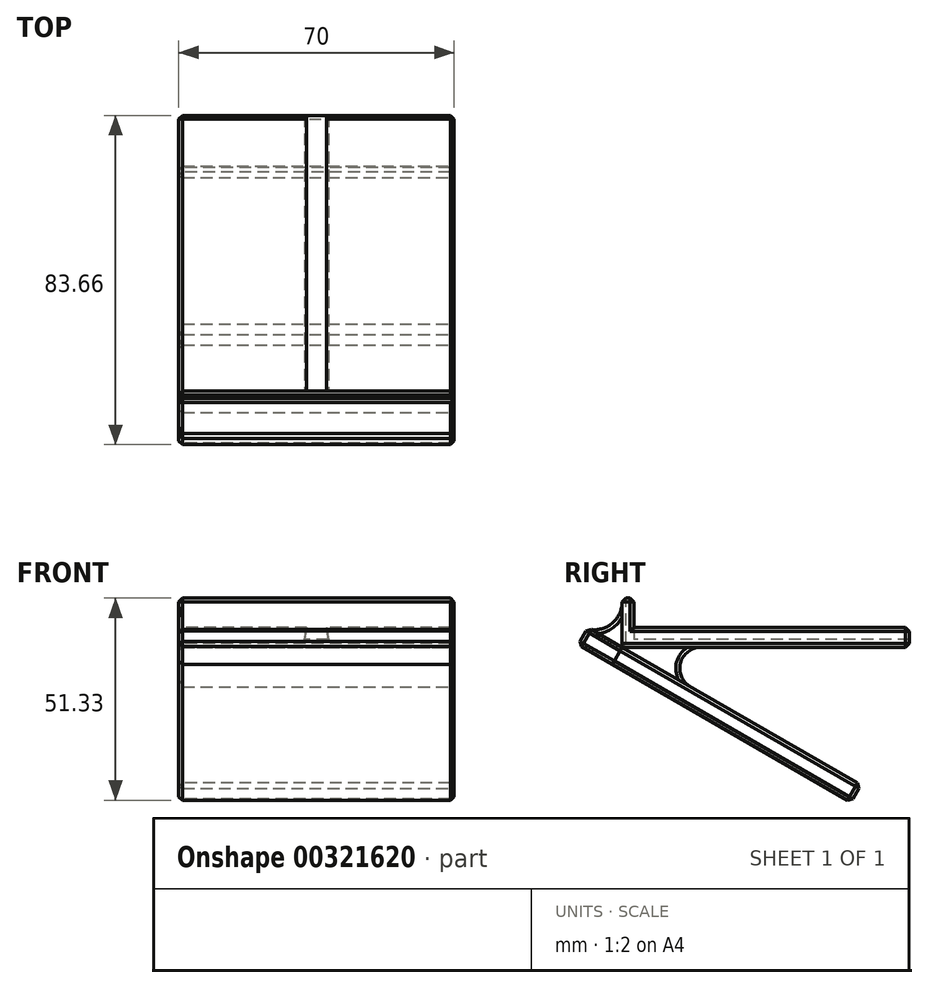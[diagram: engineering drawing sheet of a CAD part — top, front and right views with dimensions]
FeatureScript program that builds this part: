
annotation { "Feature Type Name" : "Feature", "Feature Type Description" : "" }
export const myFeature = defineFeature(function(context is Context, id is Id, definition is map)
    precondition{}
    {
        {
            var Q0;
            Q0=qCreatedBy(makeId("Top.planeOp"),FACE);
            var sketch = newSketch(context, id + "F0", { "sketchPlane" : qUnion([Q0])});
            skLineSegment(sketch, "E0.bottom", {"start": v(35, 35) * mm, "end": v(-35, 35) * mm});
            skLineSegment(sketch, "E0.top", {"start": v(35, -35) * mm, "end": v(-35, -35) * mm});
            skLineSegment(sketch, "E0.left", {"start": v(35, 35) * mm, "end": v(35, -35) * mm});
            skLineSegment(sketch, "E0.right", {"start": v(-35, 35) * mm, "end": v(-35, -35) * mm});
            skPoint(sketch, "E0.middle", {"position": v(0, 0) * mm});
            skSolve(sketch);
        }
        {
            var Q0;
            Q0=makeQuery(id+"F0.imprint","IMPRINT",FACE,{"disambiguationData":[TD([[makeQuery(id+"F0.imprint","IMPRINT",EDGE,{"derivedFrom":sQuery(id+"F0.wireOp",EDGE,"E0.bottom")}),1.0]])]});
            extrude(context, id + "F1", {"entities" : qUnion([Q0]), "depth" : 5 * mm});
        }
        {
            var Q0;
            Q0=makeQuery(id+"F1.opExtrude","SWEPT_FACE",FACE,{"disambiguationData":[OSD([sQuery(id+"F0.wireOp",EDGE,"E0.top")])]});
            var sketch = newSketch(context, id + "F2", { "sketchPlane" : qUnion([Q0])});
            skLineSegment(sketch, "E1", {"start": v(0, 5) * mm, "end": v(2.5, 5) * mm});
            skLineSegment(sketch, "E2", {"start": v(0, 2) * mm, "end": v(3, 2) * mm});
            skLineSegment(sketch, "E3", {"start": v(3, 2) * mm, "end": v(2.5, 5) * mm});
            skLineSegment(sketch, "E4", {"start": v(0, 2) * mm, "end": v(-3, 2) * mm});
            skLineSegment(sketch, "E5", {"start": v(0, 5) * mm, "end": v(-2.5, 5) * mm});
            skLineSegment(sketch, "E6", {"start": v(-2.5, 5) * mm, "end": v(-3, 2) * mm});
            skSolve(sketch);
        }
        {
            var Q0;
            Q0=makeQuery(id+"F2.imprint","IMPRINT",FACE,{"disambiguationData":[TD([[makeQuery(id+"F2.imprint","IMPRINT",EDGE,{"derivedFrom":sQuery(id+"F2.wireOp",EDGE,"E1")}),1.0]])]});
            var Q1;
            Q1=makeQuery(id+"F1.opExtrude","SWEPT_FACE",FACE,{"disambiguationData":[OSD([sQuery(id+"F0.wireOp",EDGE,"E0.bottom")])]});
            extrude(context, id + "F3", {"entities" : qUnion([Q0]), "operationType" : NewBodyOperationType.REMOVE, "endBound" : BoundingType.UP_TO_SURFACE, "oppositeDirection" : true, "endBoundEntityFace" : qUnion([Q1]), "depth" : 25 * mm});
        }
        {
            var Q0;
            Q0=makeQuery(id+"F1.opExtrude","SWEPT_FACE",FACE,{"disambiguationData":[OSD([sQuery(id+"F0.wireOp",EDGE,"E0.top")])]});
            var sketch = newSketch(context, id + "F4", { "sketchPlane" : qUnion([Q0])});
            skLineSegment(sketch, "E7.bottom", {"start": v(-35, 0) * mm, "end": v(35, 0) * mm});
            skLineSegment(sketch, "E7.top", {"start": v(-35, 12.5) * mm, "end": v(35, 12.5) * mm});
            skLineSegment(sketch, "E7.left", {"start": v(-35, 0) * mm, "end": v(-35, 12.5) * mm});
            skLineSegment(sketch, "E7.right", {"start": v(35, 0) * mm, "end": v(35, 12.5) * mm});
            skSolve(sketch);
        }
        {
            var Q0;
            Q0 = qSketchRegion(id + "F4", true);
            extrude(context, id + "F5", {"entities" : qUnion([Q0]), "operationType" : NewBodyOperationType.ADD, "depth" : 3 * mm});
        }
        {
            var Q0;
            Q0=makeQuery(id+"F5.opExtrude","CAP_EDGE",EDGE,{"disambiguationData":[OSD([sQuery(id+"F4.wireOp",EDGE,"E7.bottom")])],"isStart":false});
            var Q1;
            Q1=makeQuery(id+"F5.boolean.opBoolean","MERGE",EDGE,{"derivedFrom":[makeQuery(id+"F1.opExtrude","CAP_EDGE",EDGE,{"disambiguationData":[OSD([sQuery(id+"F0.wireOp",EDGE,"E0.left")])],"isStart":true}),makeQuery(id+"F5.opExtrude","SWEPT_EDGE",EDGE,{"disambiguationData":[OSD([sQuery(id+"F4.wireOp",EDGE,"E7.bottom"),sQuery(id+"F4.wireOp",EDGE,"E7.right")])]})]});
            cPlane(context, id + "F6", {"entities" : qUnion([Q0, Q1]), "cplaneType" : CPlaneType.LINE_ANGLE, "offset" : 25 * mm, "angle" : 30 * degree, "width" : 150 * mm, "height" : 150 * mm});
        }
        {
            var Q0;
            Q0=qCreatedBy(id+"F6.planeOp",FACE);
            var sketch = newSketch(context, id + "F7", { "sketchPlane" : qUnion([Q0])});
            skLineSegment(sketch, "E8.bottom", {"start": v(-35, -32.9) * mm, "end": v(35, -32.9) * mm});
            skLineSegment(sketch, "E8.top", {"start": v(-35, 37.1) * mm, "end": v(35, 37.1) * mm});
            skLineSegment(sketch, "E8.left", {"start": v(-35, -32.9) * mm, "end": v(-35, 37.1) * mm});
            skLineSegment(sketch, "E8.right", {"start": v(35, -32.9) * mm, "end": v(35, 37.1) * mm});
            skSolve(sketch);
        }
        {
            var Q0;
            Q0 = qSketchRegion(id + "F7", true);
            extrude(context, id + "F8", {"entities" : qUnion([Q0]), "operationType" : NewBodyOperationType.ADD, "oppositeDirection" : true, "depth" : 5 * mm});
        }
        {
            var Q0;
            Q0=makeQuery(id+"F8.opExtrude","SWEPT_FACE",FACE,{"disambiguationData":[OSD([sQuery(id+"F7.wireOp",EDGE,"E8.bottom")])]});
            extrude(context, id + "F9", {"entities" : qUnion([Q0]), "depth" : 10 * mm});
        }
        {
            var Q0;
            Q0=makeQuery(id+"F8.opExtrude","SWEPT_FACE",FACE,{"disambiguationData":[OSD([sQuery(id+"F7.wireOp",EDGE,"E8.right")])]});
            var sketch = newSketch(context, id + "F10", { "sketchPlane" : qUnion([Q0])});
            skLineSegment(sketch, "E9", {"start": v(-38, 0) * mm, "end": v(-20.68, -10) * mm});
            skLineSegment(sketch, "E10", {"start": v(-18, 0) * mm, "end": v(-38, 0) * mm});
            skLineSegment(sketch, "E11", {"start": v(-38, 0) * mm, "end": v(-45.8, 4.5) * mm});
            skLineSegment(sketch, "E12", {"start": v(-38, 0) * mm, "end": v(-38, 11.5) * mm});
            skArc(sketch, "E13", {"start": v(-45.8, 4.5) * mm, "mid": v(-40.34, 6.26) * mm, "end": v(-38, 11.5) * mm});
            skArc(sketch, "E14", {"start": v(-18, 0) * mm, "mid": v(-23.18, -3.97) * mm, "end": v(-20.68, -10) * mm});
            skSolve(sketch);
        }
        {
            var Q0;
            Q0 = qSketchRegion(id + "F10", true);
            var Q1;
            Q1=makeQuery(id+"F8.opExtrude","SWEPT_FACE",FACE,{"disambiguationData":[OSD([sQuery(id+"F7.wireOp",EDGE,"E8.left")])]});
            extrude(context, id + "F11", {"entities" : qUnion([Q0]), "endBound" : BoundingType.UP_TO_SURFACE, "oppositeDirection" : true, "endBoundEntityFace" : qUnion([Q1]), "depth" : 25 * mm});
        }
        {
            var Q0;
            Q0=makeQuery(id+"F9.opExtrude","CAP_EDGE",EDGE,{"disambiguationData":[OSD([sQuery(id+"F7.wireOp",EDGE,"E8.bottom"),sQuery(id+"F7.wireOp",EDGE,"E8.right")])],"isStart":false});
            var Q1;
            {var subQ0=sQuery(id+"F7.wireOp",EDGE,"E8.right");var subQ1=sQuery(id+"F7.wireOp",EDGE,"E8.bottom");Q1=makeQuery(id+"F9.opExtrude","SWEPT_EDGE",EDGE,{"disambiguationData":[OSD([subQ1,subQ0]),TDD([makeQuery(id+"F8.opExtrude","CAP_VERTEX",VERTEX,{"disambiguationData":[OSD([subQ1,subQ0])],"isStart":false})])]});}
            var Q2;
            Q2=makeQuery(id+"F8.opExtrude","CAP_EDGE",EDGE,{"disambiguationData":[OSD([sQuery(id+"F7.wireOp",EDGE,"E8.right")])],"isStart":false});
            var Q3;
            Q3=makeQuery(id+"F5.opExtrude","SWEPT_EDGE",EDGE,{"disambiguationData":[OSD([sQuery(id+"F4.wireOp",EDGE,"E7.top"),sQuery(id+"F4.wireOp",EDGE,"E7.right")])]});
            var Q4;
            Q4=makeQuery(id+"F5.opExtrude","CAP_EDGE",EDGE,{"disambiguationData":[OSD([sQuery(id+"F4.wireOp",EDGE,"E7.right")])],"isStart":true});
            var Q5;
            Q5=makeQuery(id+"F1.opExtrude","CAP_EDGE",EDGE,{"disambiguationData":[OSD([sQuery(id+"F0.wireOp",EDGE,"E0.left")])],"isStart":false});
            var Q6;
            Q6=makeQuery(id+"F1.opExtrude","SWEPT_EDGE",EDGE,{"disambiguationData":[OSD([sQuery(id+"F0.wireOp",EDGE,"E0.bottom"),sQuery(id+"F0.wireOp",EDGE,"E0.left")])]});
            var Q7;
            Q7=makeQuery(id+"F8.opExtrude","SWEPT_EDGE",EDGE,{"disambiguationData":[OSD([sQuery(id+"F7.wireOp",EDGE,"E8.top"),sQuery(id+"F7.wireOp",EDGE,"E8.right")])]});
            var Q8;
            Q8=makeQuery(id+"F5.opExtrude","CAP_EDGE",EDGE,{"disambiguationData":[OSD([sQuery(id+"F4.wireOp",EDGE,"E7.top")])],"isStart":false});
            var Q9;
            Q9=makeQuery(id+"F5.opExtrude","SWEPT_FACE",FACE,{"disambiguationData":[OSD([sQuery(id+"F4.wireOp",EDGE,"E7.top")])]});
            var Q10;
            {var subQ0=sQuery(id+"F7.wireOp",EDGE,"E8.bottom");Q10=makeQuery(id+"F9.opExtrude","CAP_EDGE",EDGE,{"disambiguationData":[OSD([subQ0]),TDD([makeQuery(id+"F8.opExtrude","CAP_EDGE",EDGE,{"disambiguationData":[OSD([subQ0])],"isStart":true})])],"isStart":false});}
            var Q11;
            {var subQ0=sQuery(id+"F7.wireOp",EDGE,"E8.bottom");Q11=makeQuery(id+"F9.opExtrude","CAP_EDGE",EDGE,{"disambiguationData":[OSD([subQ0]),TDD([makeQuery(id+"F8.opExtrude","CAP_EDGE",EDGE,{"disambiguationData":[OSD([subQ0])],"isStart":false})])],"isStart":false});}
            var Q12;
            Q12=makeQuery(id+"F9.opExtrude","CAP_EDGE",EDGE,{"disambiguationData":[OSD([sQuery(id+"F7.wireOp",EDGE,"E8.bottom"),sQuery(id+"F7.wireOp",EDGE,"E8.left")])],"isStart":false});
            var Q13;
            {var subQ0=sQuery(id+"F7.wireOp",EDGE,"E8.left");var subQ1=sQuery(id+"F7.wireOp",EDGE,"E8.bottom");Q13=makeQuery(id+"F9.opExtrude","SWEPT_EDGE",EDGE,{"disambiguationData":[OSD([subQ1,subQ0]),TDD([makeQuery(id+"F8.opExtrude","CAP_VERTEX",VERTEX,{"disambiguationData":[OSD([subQ1,subQ0])],"isStart":false})])]});}
            var Q14;
            Q14=makeQuery(id+"F8.opExtrude","CAP_EDGE",EDGE,{"disambiguationData":[OSD([sQuery(id+"F7.wireOp",EDGE,"E8.left")])],"isStart":false});
            var Q15;
            Q15=makeQuery(id+"F5.opExtrude","CAP_EDGE",EDGE,{"disambiguationData":[OSD([sQuery(id+"F4.wireOp",EDGE,"E7.left")])],"isStart":true});
            var Q16;
            Q16=makeQuery(id+"F1.opExtrude","CAP_EDGE",EDGE,{"disambiguationData":[OSD([sQuery(id+"F0.wireOp",EDGE,"E0.right")])],"isStart":false});
            var Q17;
            Q17=makeQuery(id+"F1.opExtrude","SWEPT_EDGE",EDGE,{"disambiguationData":[OSD([sQuery(id+"F0.wireOp",EDGE,"E0.bottom"),sQuery(id+"F0.wireOp",EDGE,"E0.right")])]});
            var Q18;
            Q18=makeQuery(id+"F8.opExtrude","SWEPT_EDGE",EDGE,{"disambiguationData":[OSD([sQuery(id+"F7.wireOp",EDGE,"E8.top"),sQuery(id+"F7.wireOp",EDGE,"E8.left")])]});
            var Q19;
            Q19=makeQuery(id+"F8.opExtrude","CAP_EDGE",EDGE,{"disambiguationData":[OSD([sQuery(id+"F7.wireOp",EDGE,"E8.top")])],"isStart":false});
            var Q20;
            Q20=makeQuery(id+"F8.opExtrude","SWEPT_FACE",FACE,{"disambiguationData":[OSD([sQuery(id+"F7.wireOp",EDGE,"E8.top")])]});
            var Q21;
            Q21=makeQuery(id+"F1.opExtrude","CAP_EDGE",EDGE,{"disambiguationData":[OSD([sQuery(id+"F0.wireOp",EDGE,"E0.bottom")])],"isStart":true});
            var Q22;
            {var subQ0=sQuery(id+"F0.wireOp",EDGE,"E0.bottom");var subQ1=sQuery(id+"F0.wireOp",EDGE,"E0.left");Q22=makeQuery(id+"F3.boolean.opBoolean","SPLIT",EDGE,{"disambiguationData":[TD([makeQuery(id+"F1.opExtrude","SWEPT_FACE",FACE,{"disambiguationData":[OSD([subQ1])]})])],"derivedFrom":makeQuery(id+"F1.opExtrude","CAP_EDGE",EDGE,{"disambiguationData":[OSD([subQ0])],"isStart":false})});}
            var Q23;
            {var subQ0=sQuery(id+"F0.wireOp",EDGE,"E0.bottom");var subQ1=sQuery(id+"F0.wireOp",EDGE,"E0.right");Q23=makeQuery(id+"F3.boolean.opBoolean","SPLIT",EDGE,{"disambiguationData":[TD([makeQuery(id+"F1.opExtrude","SWEPT_FACE",FACE,{"disambiguationData":[OSD([subQ1])]})])],"derivedFrom":makeQuery(id+"F1.opExtrude","CAP_EDGE",EDGE,{"disambiguationData":[OSD([subQ0])],"isStart":false})});}
            var Q24;
            Q24=makeQuery(id+"F11.opExtrude","CAP_EDGE",EDGE,{"disambiguationData":[OSD([sQuery(id+"F10.wireOp",EDGE,"E13")])],"isStart":true});
            var Q25;
            Q25=makeQuery(id+"F11.opExtrude","CAP_EDGE",EDGE,{"disambiguationData":[OSD([sQuery(id+"F10.wireOp",EDGE,"E14")])],"isStart":true});
            var Q26;
            Q26=makeQuery(id+"F11.opExtrude","CAP_EDGE",EDGE,{"disambiguationData":[OSD([sQuery(id+"F10.wireOp",EDGE,"E13")])],"isStart":false});
            var Q27;
            Q27=makeQuery(id+"F11.opExtrude","CAP_EDGE",EDGE,{"disambiguationData":[OSD([sQuery(id+"F10.wireOp",EDGE,"E14")])],"isStart":false});
            var Q28;
            {var subQ0=sQuery(id+"F7.wireOp",EDGE,"E8.left");var subQ1=sQuery(id+"F7.wireOp",EDGE,"E8.bottom");Q28=makeQuery(id+"F9.opExtrude","SWEPT_EDGE",EDGE,{"disambiguationData":[OSD([subQ1,subQ0]),TDD([makeQuery(id+"F8.opExtrude","CAP_VERTEX",VERTEX,{"disambiguationData":[OSD([subQ1,subQ0])],"isStart":true})])]});}
            var Q29;
            Q29=makeQuery(id+"F8.opExtrude","CAP_EDGE",EDGE,{"disambiguationData":[OSD([sQuery(id+"F7.wireOp",EDGE,"E8.left")])],"isStart":true});
            var Q30;
            Q30=makeQuery(id+"F5.opExtrude","CAP_EDGE",EDGE,{"disambiguationData":[OSD([sQuery(id+"F4.wireOp",EDGE,"E7.left")])],"isStart":false});
            var Q31;
            Q31=makeQuery(id+"F5.boolean.opBoolean","MERGE",EDGE,{"derivedFrom":[makeQuery(id+"F1.opExtrude","CAP_EDGE",EDGE,{"disambiguationData":[OSD([sQuery(id+"F0.wireOp",EDGE,"E0.right")])],"isStart":true}),makeQuery(id+"F5.opExtrude","SWEPT_EDGE",EDGE,{"disambiguationData":[OSD([sQuery(id+"F4.wireOp",EDGE,"E7.bottom"),sQuery(id+"F4.wireOp",EDGE,"E7.left")])]})]});
            var Q32;
            {var subQ0=sQuery(id+"F7.wireOp",EDGE,"E8.right");var subQ1=sQuery(id+"F7.wireOp",EDGE,"E8.bottom");Q32=makeQuery(id+"F9.opExtrude","SWEPT_EDGE",EDGE,{"disambiguationData":[OSD([subQ1,subQ0]),TDD([makeQuery(id+"F8.opExtrude","CAP_VERTEX",VERTEX,{"disambiguationData":[OSD([subQ1,subQ0])],"isStart":true})])]});}
            var Q33;
            Q33=makeQuery(id+"F8.opExtrude","CAP_EDGE",EDGE,{"disambiguationData":[OSD([sQuery(id+"F7.wireOp",EDGE,"E8.right")])],"isStart":true});
            var Q34;
            Q34=makeQuery(id+"F5.boolean.opBoolean","MERGE",EDGE,{"derivedFrom":[makeQuery(id+"F1.opExtrude","CAP_EDGE",EDGE,{"disambiguationData":[OSD([sQuery(id+"F0.wireOp",EDGE,"E0.left")])],"isStart":true}),makeQuery(id+"F5.opExtrude","SWEPT_EDGE",EDGE,{"disambiguationData":[OSD([sQuery(id+"F4.wireOp",EDGE,"E7.bottom"),sQuery(id+"F4.wireOp",EDGE,"E7.right")])]})]});
            chamfer(context, id + "F12", {"entities" : qUnion([Q0, Q1, Q2, Q3, Q4, Q5, Q6, Q7, Q8, Q9, Q10, Q11, Q12, Q13, Q14, Q15, Q16, Q17, Q18, Q19, Q20, Q21, Q22, Q23, Q24, Q25, Q26, Q27, Q28, Q29, Q30, Q31, Q32, Q33, Q34]), "width" : 1 * mm});
        }
    });
